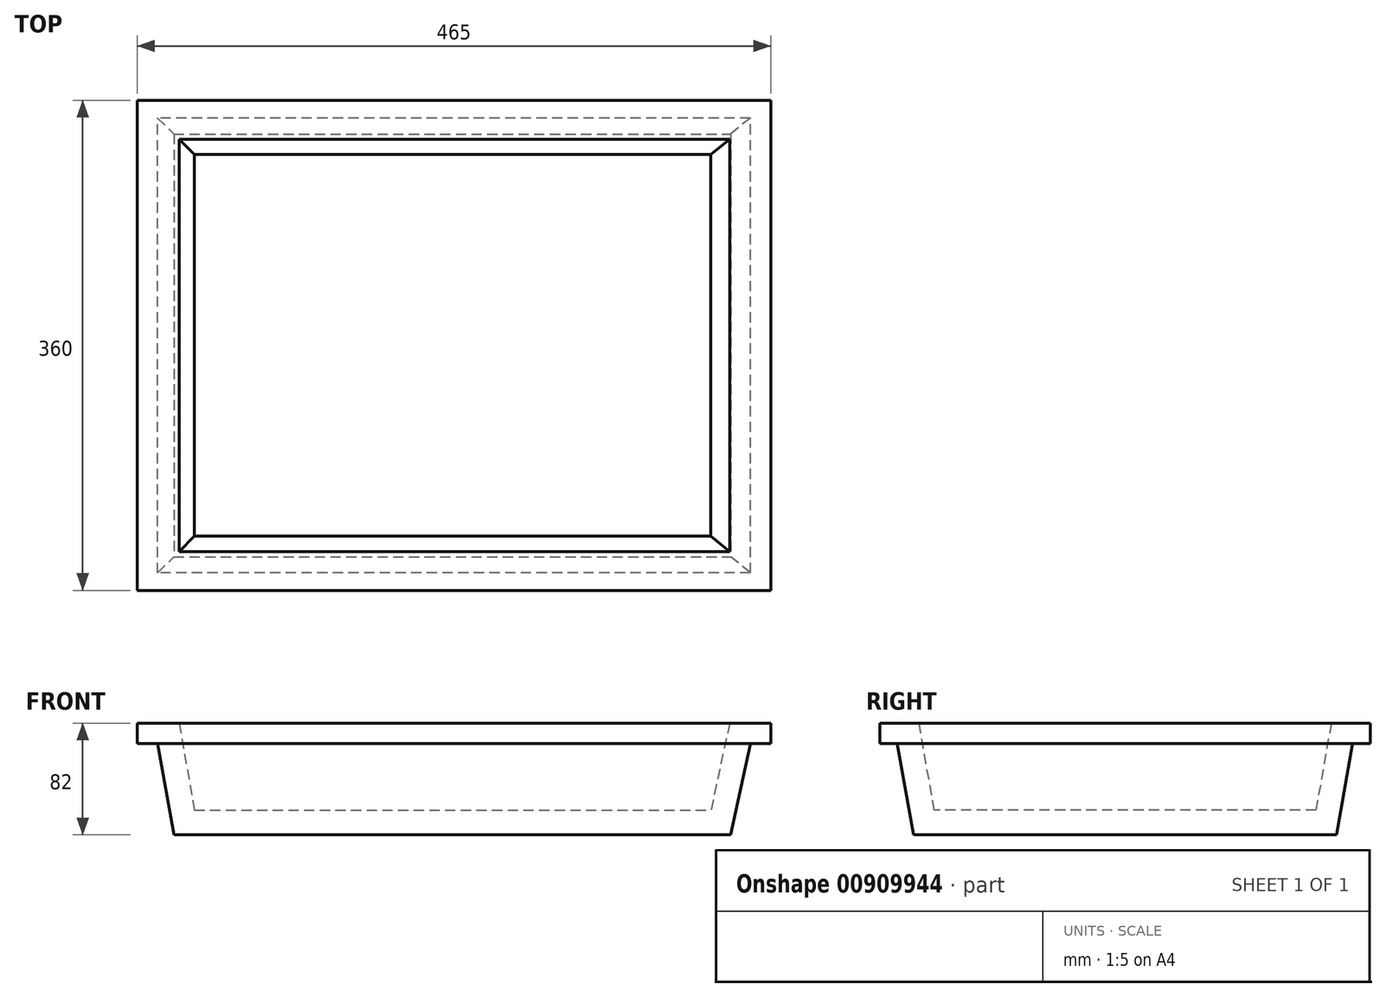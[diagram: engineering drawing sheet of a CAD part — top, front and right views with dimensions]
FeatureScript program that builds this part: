
annotation { "Feature Type Name" : "Feature", "Feature Type Description" : "" }
export const myFeature = defineFeature(function(context is Context, id is Id, definition is map)
    precondition{}
    {
        {
            var Q0;
            Q0=qCreatedBy(makeId("Top.planeOp"),FACE);
            var sketch = newSketch(context, id + "F0", { "sketchPlane" : qUnion([Q0])});
            skLineSegment(sketch, "E0.bottom", {"start": v(-226.16, -180) * mm, "end": v(238.84, -180) * mm});
            skLineSegment(sketch, "E0.top", {"start": v(-226.16, 180) * mm, "end": v(238.84, 180) * mm});
            skLineSegment(sketch, "E0.left", {"start": v(-226.16, -180) * mm, "end": v(-226.16, 180) * mm});
            skLineSegment(sketch, "E0.right", {"start": v(238.84, -180) * mm, "end": v(238.84, 180) * mm});
            skSolve(sketch);
        }
        {
            var Q0;
            Q0 = qSketchRegion(id + "F0", true);
            extrude(context, id + "F1", {"entities" : qUnion([Q0]), "oppositeDirection" : true, "depth" : 82 * mm, "offsetDistance" : 25 * mm});
        }
        {
            var Q0;
            Q0=qCreatedBy(makeId("Right.planeOp"),FACE);
            var sketch = newSketch(context, id + "F2", { "sketchPlane" : qUnion([Q0])});
            skLineSegment(sketch, "E1", {"start": v(-210, -112) * mm, "end": v(-150, -112) * mm});
            skLineSegment(sketch, "E2", {"start": v(-150, -112) * mm, "end": v(-167.1, -15) * mm});
            skLineSegment(sketch, "E3", {"start": v(-167.1, -15) * mm, "end": v(-210, -15) * mm});
            skLineSegment(sketch, "E4", {"start": v(-210, -15) * mm, "end": v(-210, -112) * mm});
            skLineSegment(sketch, "E5.MirrorCS", {"start": v(167.1, -15) * mm, "end": v(210, -15) * mm});
            skLineSegment(sketch, "E6.MirrorCS", {"start": v(150, -112) * mm, "end": v(167.1, -15) * mm});
            skLineSegment(sketch, "E7.MirrorCS", {"start": v(210, -15) * mm, "end": v(210, -112) * mm});
            skLineSegment(sketch, "E8.MirrorCS", {"start": v(210, -112) * mm, "end": v(150, -112) * mm});
            skSolve(sketch);
        }
        {
            var Q0;
            Q0=makeQuery(id+"F2.imprint","IMPRINT",FACE,{"disambiguationData":[TD([[makeQuery(id+"F2.imprint","IMPRINT",EDGE,{"derivedFrom":sQuery(id+"F2.wireOp",EDGE,"E1")}),1.0]])]});
            var Q1;
            Q1=makeQuery(id+"F2.imprint","IMPRINT",FACE,{"disambiguationData":[TD([[makeQuery(id+"F2.imprint","IMPRINT",EDGE,{"derivedFrom":sQuery(id+"F2.wireOp",EDGE,"E5.MirrorCS")}),-1.0]])]});
            extrude(context, id + "F3", {"entities" : qUnion([Q0, Q1]), "operationType" : NewBodyOperationType.REMOVE, "endBound" : BoundingType.THROUGH_ALL, "depth" : 25 * mm, "offsetDistance" : 25 * mm, "hasSecondDirection" : true, "secondDirectionOppositeDirection" : true, "secondDirectionDepth" : 251 * mm});
        }
        {
            var Q0;
            Q0=qCreatedBy(makeId("Front.planeOp"),FACE);
            var sketch = newSketch(context, id + "F4", { "sketchPlane" : qUnion([Q0])});
            skLineSegment(sketch, "E9", {"start": v(-241.16, -185.14) * mm, "end": v(-181.16, -185.14) * mm});
            skLineSegment(sketch, "E10", {"start": v(-181.16, -185.14) * mm, "end": v(-211.16, -15) * mm});
            skLineSegment(sketch, "E11", {"start": v(-211.16, -15) * mm, "end": v(-241.16, -15) * mm});
            skLineSegment(sketch, "E12", {"start": v(-241.16, -15) * mm, "end": v(-241.16, -185.14) * mm});
            skLineSegment(sketch, "E13.MirrorCS", {"start": v(223.84, -15) * mm, "end": v(253.84, -15) * mm});
            skLineSegment(sketch, "E14.MirrorCS", {"start": v(193.88, -154.36) * mm, "end": v(223.84, -15) * mm});
            skLineSegment(sketch, "E15.MirrorCS", {"start": v(253.84, -15) * mm, "end": v(253.84, -156.6) * mm});
            skLineSegment(sketch, "E16.MirrorCS", {"start": v(253.84, -156.6) * mm, "end": v(193.88, -154.36) * mm});
            skSolve(sketch);
        }
        {
            var Q0;
            Q0 = qSketchRegion(id + "F4", true);
            extrude(context, id + "F5", {"entities" : qUnion([Q0]), "operationType" : NewBodyOperationType.REMOVE, "depth" : 190 * mm, "offsetDistance" : 25 * mm, "hasSecondDirection" : true, "secondDirectionOppositeDirection" : true, "secondDirectionDepth" : 341 * mm});
        }
        {
            var Q0;
            Q0=makeQuery(id+"F1.opExtrude","CAP_FACE",FACE,{"disambiguationData":[OSD([sQuery(id+"F0.wireOp",EDGE,"E0.bottom"),sQuery(id+"F0.wireOp",EDGE,"E0.top"),sQuery(id+"F0.wireOp",EDGE,"E0.left"),sQuery(id+"F0.wireOp",EDGE,"E0.right")])],"isStart":true});
            shell(context, id + "F6", {"entities" : qUnion([Q0]), "thickness" : 18 * mm});
        }
    });
